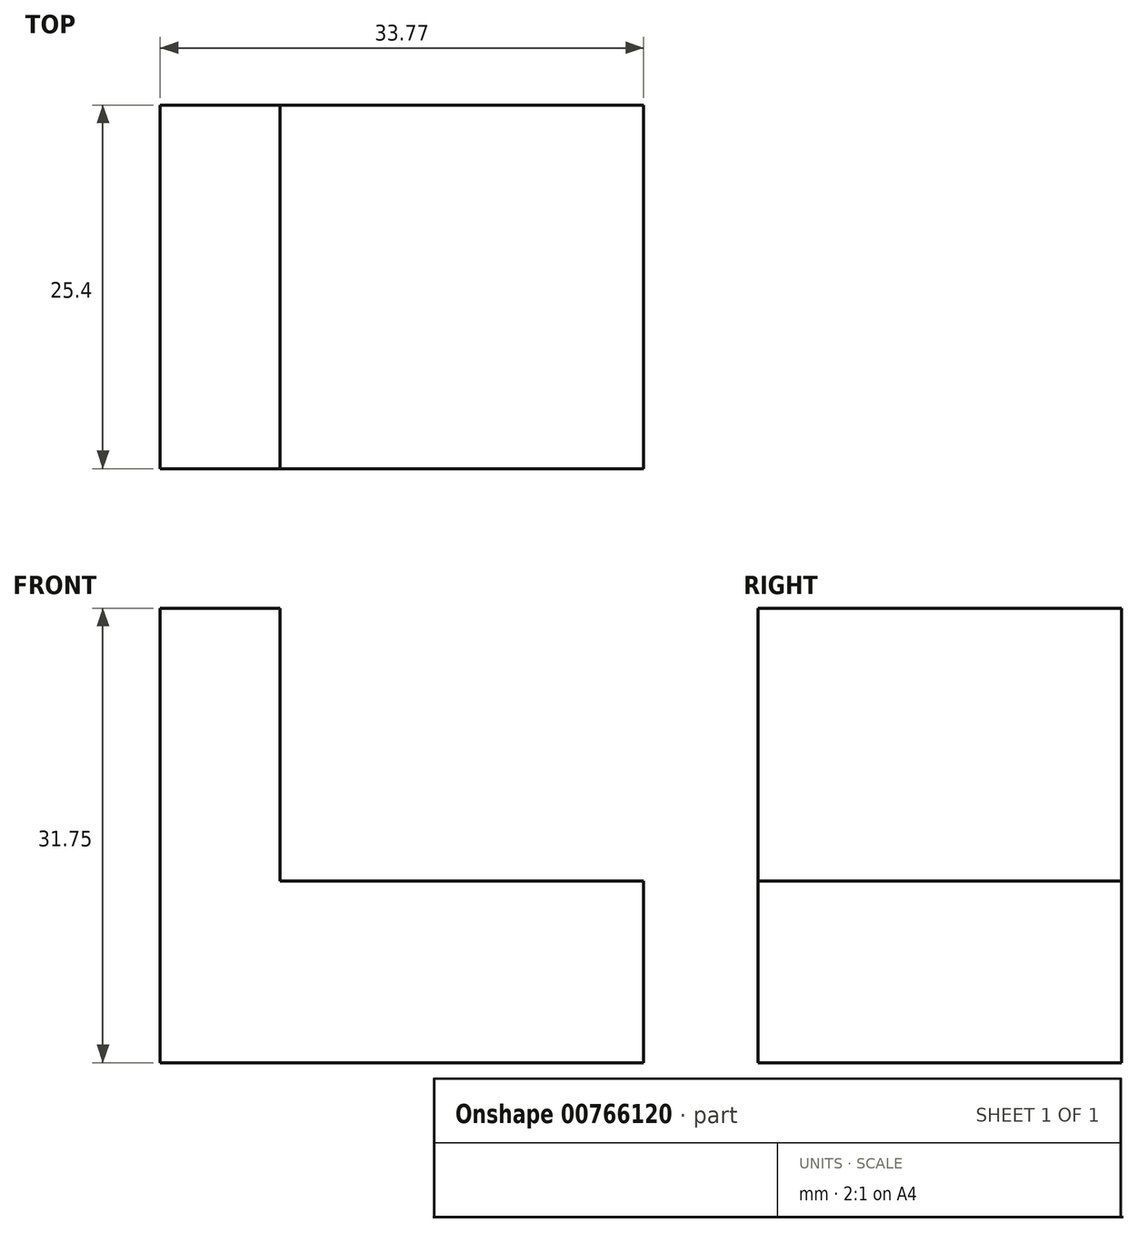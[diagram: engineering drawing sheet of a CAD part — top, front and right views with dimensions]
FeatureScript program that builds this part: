
annotation { "Feature Type Name" : "Feature", "Feature Type Description" : "" }
export const myFeature = defineFeature(function(context is Context, id is Id, definition is map)
    precondition{}
    {
        {
            var Q0;
            Q0=qCreatedBy(makeId("Front.planeOp"),FACE);
            var sketch = newSketch(context, id + "F0", { "sketchPlane" : qUnion([Q0])});
            skLineSegment(sketch, "E0", {"start": v(0, 0) * mm, "end": v(33.77, 0) * mm});
            skLineSegment(sketch, "E1", {"start": v(33.77, 0) * mm, "end": v(33.77, 12.7) * mm});
            skLineSegment(sketch, "E2", {"start": v(33.77, 12.7) * mm, "end": v(8.37, 12.7) * mm});
            skLineSegment(sketch, "E3", {"start": v(8.37, 12.7) * mm, "end": v(8.37, 31.75) * mm});
            skLineSegment(sketch, "E4", {"start": v(8.37, 31.75) * mm, "end": v(0, 31.75) * mm});
            skLineSegment(sketch, "E5", {"start": v(0, 31.75) * mm, "end": v(0, 0) * mm});
            skSolve(sketch);
        }
        {
            var Q0;
            Q0 = qSketchRegion(id + "F0", true);
            extrude(context, id + "F1", {"entities" : qUnion([Q0]), "depth" : 25.4 * mm, "offsetDistance" : 25.4 * mm});
        }
    });
